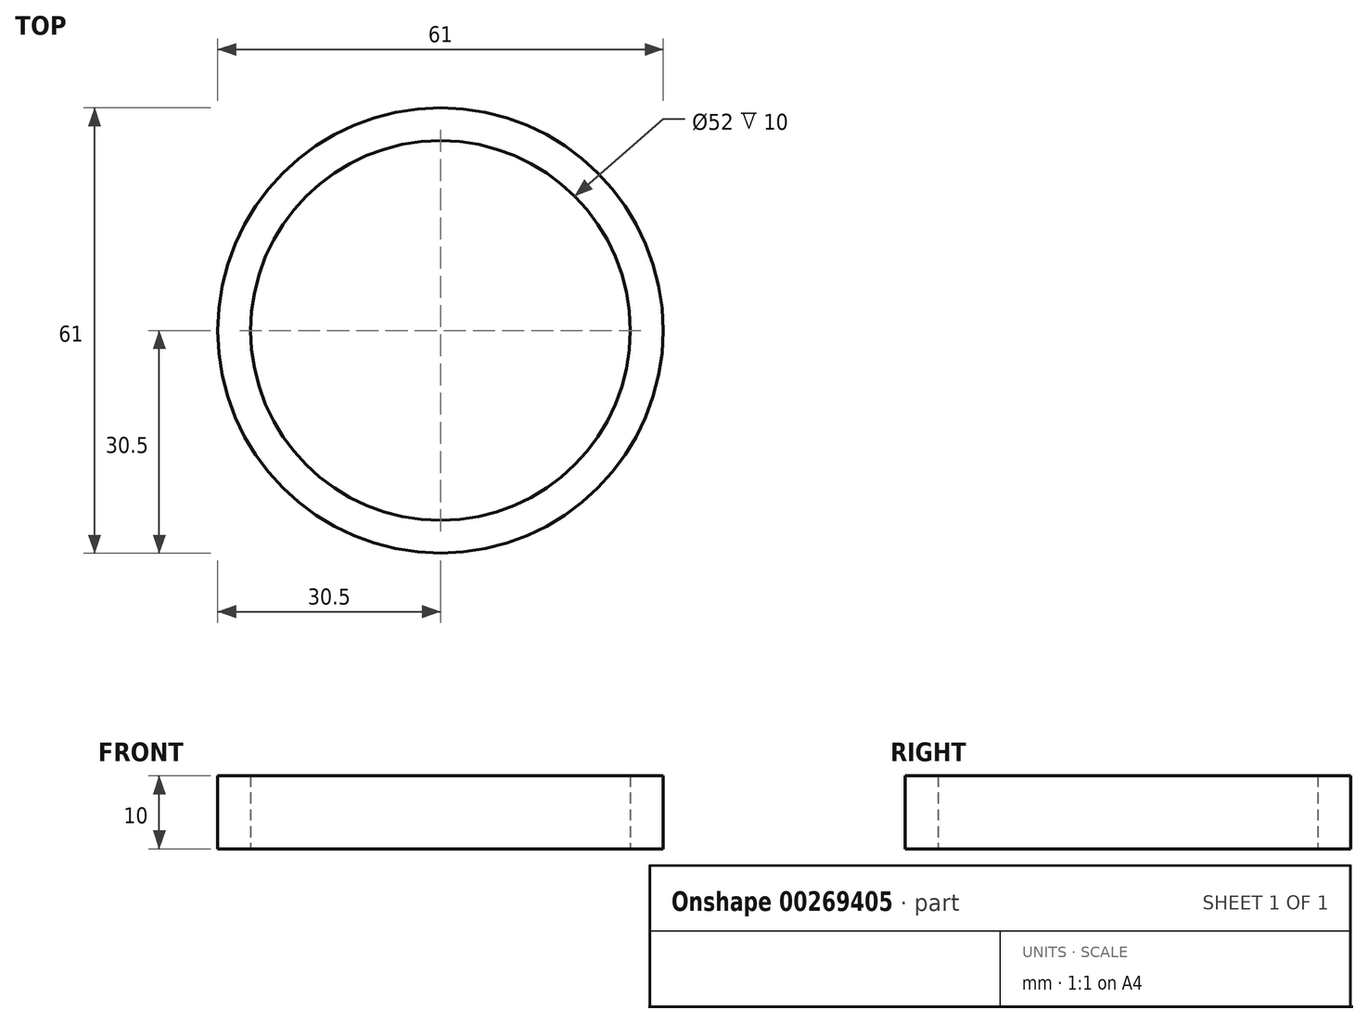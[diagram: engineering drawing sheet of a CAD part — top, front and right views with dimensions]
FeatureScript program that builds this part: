
annotation { "Feature Type Name" : "Feature", "Feature Type Description" : "" }
export const myFeature = defineFeature(function(context is Context, id is Id, definition is map)
    precondition{}
    {
        {
            var Q0;
            Q0=qCreatedBy(makeId("Top.planeOp"),FACE);
            var sketch = newSketch(context, id + "F0", { "sketchPlane" : qUnion([Q0])});
            skCircle(sketch, "E0", {"center": v(0, 0) * mm, "radius": 26 * mm});
            skCircle(sketch, "E1", {"center": v(0, 0) * mm, "radius": 40 * mm});
            skCircle(sketch, "E2", {"center": v(0, 0) * mm, "radius": 30.5 * mm});
            skCircle(sketch, "E3", {"center": v(0, 0) * mm, "radius": 35.5 * mm});
            skSolve(sketch);
        }
        {
            var Q0;
            Q0=makeQuery(id+"F0.imprint","IMPRINT",FACE,{"disambiguationData":[TD([[makeQuery(id+"F0.imprint","IMPRINT",EDGE,{"derivedFrom":sQuery(id+"F0.wireOp",EDGE,"E1")}),1.0]])]});
            var Q1;
            Q1=makeQuery(id+"F0.imprint","IMPRINT",FACE,{"disambiguationData":[TD([[makeQuery(id+"F0.imprint","IMPRINT",EDGE,{"derivedFrom":sQuery(id+"F0.wireOp",EDGE,"E0")}),-1.0]])]});
            extrude(context, id + "F1", {"entities" : qUnion([Q0, Q1]), "depth" : 10 * mm});
        }
        {
            var Q0;
            Q0=makeQuery(id+"F1.opExtrude","SWEPT_BODY",BODY,{"disambiguationData":[OSD([sQuery(id+"F0.wireOp",EDGE,"E1"),sQuery(id+"F0.wireOp",EDGE,"E3")])]});
            deleteBodies(context, id + "F2", {"entities" : qUnion([Q0])});
        }
    });
